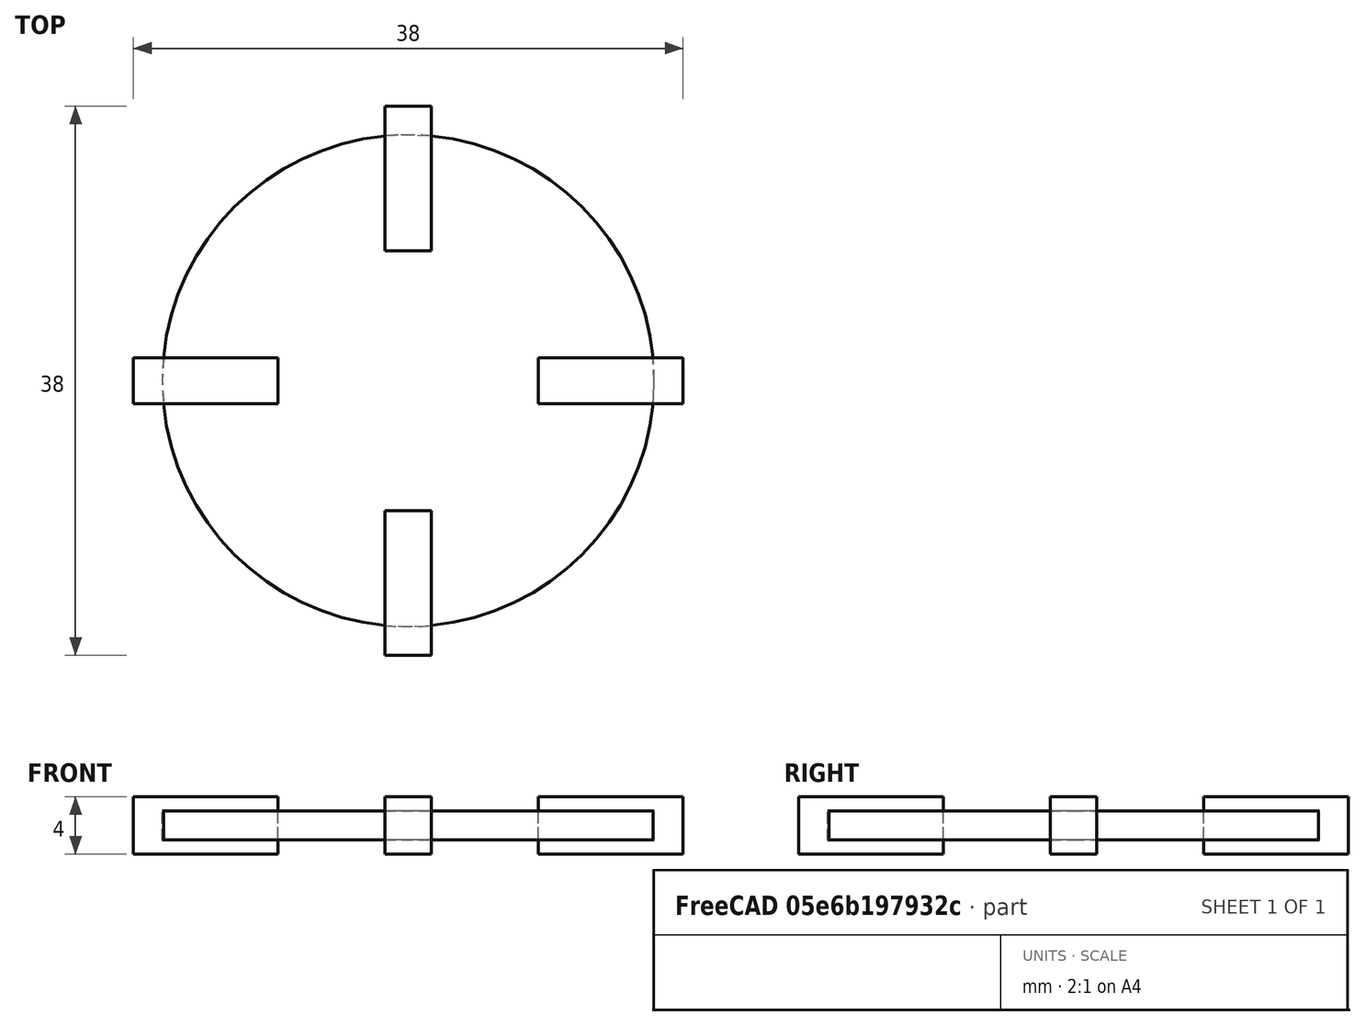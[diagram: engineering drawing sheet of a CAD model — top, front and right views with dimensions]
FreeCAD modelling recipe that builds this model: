
FCSTD DOCUMENT  (FreeCAD 0.14R3702 (Git))
Label: union
License: CC-BY 3.0
LicenseURL: http://creativecommons.org/licenses/by/3.0/
objects: Part::Cylinder×1, Part::Box×1, Part::FeaturePython×1, Part::Cut×1, Part::Part2DObjectPython×1
note: 5 computed .brp shape members not serialized (recipe doc carries the construction recipe); baked Part::Feature solids carry a one-line shape summary decoded from their .brp

FEATURE [Part::Cylinder] Cylinder  label="Cilindro"
  Angle = 360
  Height = 2
  Radius = 17
FEATURE [Part::Box] Box  label="Cubo"
  Height = 4
  Length = 3.2
  Placement = pos=(-1.6,9,-1) rot=(0,0,1;0rad)
  Width = 10
FEATURE [Part::FeaturePython] Array  # Draft array (typed FeaturePython)
  Angle = 360
  ArrayType = 1
  Axis = (0,0,1)
  Base = -> Box
  Center = (0,0,0)
  IntervalX = (1,0,0)
  IntervalY = (0,1,0)
  IntervalZ = (0,0,1)
  NumberPolar = 4
  NumberX = 2
  NumberY = 2
  NumberZ = 1
FEATURE [Part::Cut] Cut
  Base = -> Cylinder
  Tool = -> Array
FEATURE [Part::Part2DObjectPython] Shape2DView  # Draft 2D object (typed FeaturePython)
  Base = -> Cut
  HiddenLines = false
  Projection = (0,0,1)
  ProjectionMode = 0
  SegmentLength = 0.05
  Tessellation = false
